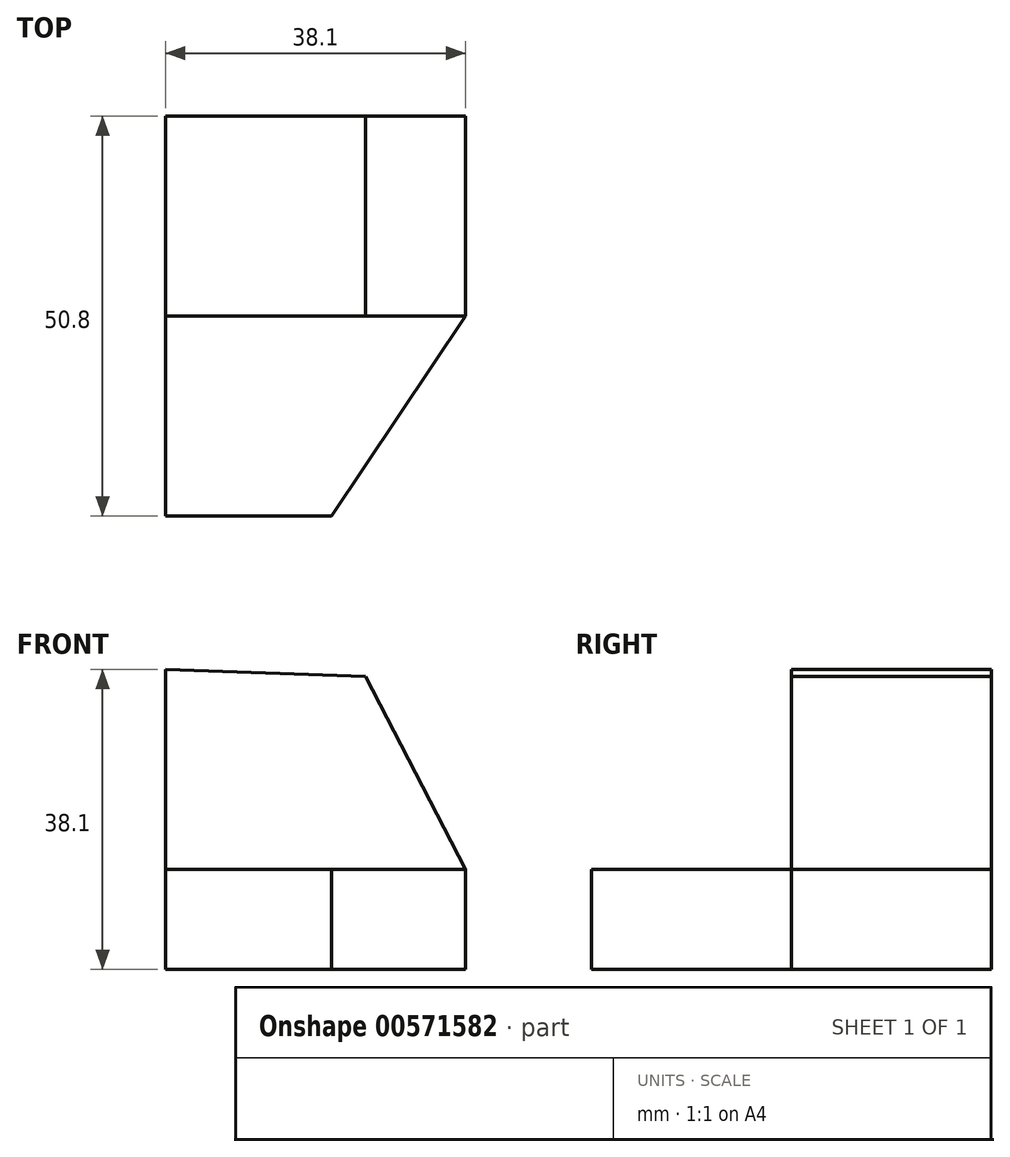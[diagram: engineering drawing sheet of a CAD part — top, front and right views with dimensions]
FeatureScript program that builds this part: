
annotation { "Feature Type Name" : "Feature", "Feature Type Description" : "" }
export const myFeature = defineFeature(function(context is Context, id is Id, definition is map)
    precondition{}
    {
        {
            var Q0;
            Q0=qCreatedBy(makeId("Front.planeOp"),FACE);
            var sketch = newSketch(context, id + "F0", { "sketchPlane" : qUnion([Q0])});
            skLineSegment(sketch, "E0", {"start": v(-58.7, 50.35) * mm, "end": v(-58.7, 12.25) * mm});
            skLineSegment(sketch, "E1", {"start": v(-58.7, 12.25) * mm, "end": v(-20.6, 12.25) * mm});
            skLineSegment(sketch, "E2", {"start": v(-20.6, 12.25) * mm, "end": v(-20.6, 24.95) * mm});
            skLineSegment(sketch, "E3", {"start": v(-20.6, 24.95) * mm, "end": v(-33.32, 49.47) * mm});
            skLineSegment(sketch, "E4", {"start": v(-33.32, 49.47) * mm, "end": v(-58.7, 50.35) * mm});
            skSolve(sketch);
        }
        {
            var Q0;
            Q0=makeQuery(id+"F0.imprint","IMPRINT",FACE,{"disambiguationData":[TD([[makeQuery(id+"F0.imprint","IMPRINT",EDGE,{"derivedFrom":sQuery(id+"F0.wireOp",EDGE,"E0")}),1.0]])]});
            extrude(context, id + "F1", {"entities" : qUnion([Q0]), "depth" : 25.4 * mm, "offsetDistance" : 25.4 * mm});
        }
        {
            var Q0;
            Q0=makeQuery(id+"F1.opExtrude","CAP_FACE",FACE,{"disambiguationData":[OSD([sQuery(id+"F0.wireOp",EDGE,"E0"),sQuery(id+"F0.wireOp",EDGE,"E1"),sQuery(id+"F0.wireOp",EDGE,"E2"),sQuery(id+"F0.wireOp",EDGE,"E3"),sQuery(id+"F0.wireOp",EDGE,"E4")])],"isStart":false});
            var sketch = newSketch(context, id + "F2", { "sketchPlane" : qUnion([Q0])});
            skLineSegment(sketch, "E5", {"start": v(-20.6, 24.95) * mm, "end": v(-58.7, 24.95) * mm});
            skSolve(sketch);
        }
        {
            var Q0;
            {var subQ0=sQuery(id+"F2.wireOp",EDGE,"E5");Q0=makeQuery(id+"F2.imprint","IMPRINT",FACE,{"disambiguationData":[TD([[makeQuery(id+"F2.imprint","IMPRINT",EDGE,{"derivedFrom":subQ0}),1.0]])]});}
            extrude(context, id + "F3", {"entities" : qUnion([Q0]), "operationType" : NewBodyOperationType.ADD, "depth" : 25.4 * mm, "offsetDistance" : 25.4 * mm});
        }
        {
            var Q0;
            Q0=makeQuery(id+"F3.opExtrude","SWEPT_FACE",FACE,{"disambiguationData":[OSD([sQuery(id+"F2.wireOp",EDGE,"E5")])]});
            var sketch = newSketch(context, id + "F4", { "sketchPlane" : qUnion([Q0])});
            skLineSegment(sketch, "E6", {"start": v(-20.6, -25.4) * mm, "end": v(-37.65, -50.8) * mm});
            skSolve(sketch);
        }
        {
            var Q0;
            {var subQ0=sQuery(id+"F4.wireOp",EDGE,"E6");Q0=makeQuery(id+"F4.imprint","IMPRINT",FACE,{"disambiguationData":[TD([[makeQuery(id+"F4.imprint","IMPRINT",EDGE,{"derivedFrom":subQ0}),1.0]])]});}
            extrude(context, id + "F5", {"entities" : qUnion([Q0]), "operationType" : NewBodyOperationType.REMOVE, "oppositeDirection" : true, "depth" : 25.4 * mm, "offsetDistance" : 25.4 * mm});
        }
    });
